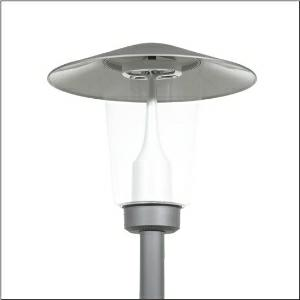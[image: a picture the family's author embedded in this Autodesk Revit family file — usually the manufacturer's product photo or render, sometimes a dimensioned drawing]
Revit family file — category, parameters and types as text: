
# Revit family: pilzleuchte_iq___st1_2a_5xa5235kf14h_dd17
name_source: partatom
category: Lighting Fixtures
units: mm (PartAtom-declared; Revit-internal decimal feet)

## family parameters
Cut with Voids When Loaded = No
Host = Face
Light Source = No
Part Type = Normal
Room Calculation Point = No
Round Connector Dimension = Use Diameter
Shared = No

## types (1)
- --- (1 x LED, 1550 lm, 10 W, 4000K)
    Apparent Load = 10 VA
    CIE Flux Codes = 24 61 93 98 100
    Color Rendering = 70
    Color Temperature = 4000K
    Default Elevation = 1800 mm
    Description = Mushroom Luminaire iQ, mast luminaire, Module 540 iQ-SR, primary light control with 3 zone facetted reflector, of plastic, silver coated, highly specular, structured, primary optical cover: cover, of PMMA, transparent, light distribution: ST1.2a, light emission: direct distribution, primary light characteristic: asymmetric, installation type: post-top, LED, High Power LED, rated luminous flux: 1.550lm, luminous efficacy: 155lm/W, light colour: 740, colour temperature: 4000K, control gear: iQ Street-Remote, control: pre-setting: logarithmic dimming characteristic, Street-Remote, Auto-Match, Temp-Guard, Lumen-Switch, Night-Set, Smart-Wire, Light-Fading, Desk-Remote (wireless, voltage-free reading and setting of iQ features in the workshop via application-optimized NFC function/RFID function), optimised constant luminous flux control (CLO 2.0), with terminal, 6-pole, max. 2.5mm², mains connection: 230..240V, AC, 50/60Hz, start of lifetime: 10W, end of service life: 10W, reduction: 5W, luminaire housing, upper part, of glass-fibre reinforced polyester, coated, Siteco® metallic grey (DB 702S), diameter: 650mm, height: 586mm, spigot size: d x l = 76 x 70mm (post-top) | with reducer (optional accessory) 60 x 70mm, mounting height: 3..5m, post-top mast mounting element, of diecast aluminium, coated, Siteco® metallic grey (DB 702S), Module 540 iQ-SR, traffic white (RAL 9016), equipment: standard, protection rating (complete): IP65, insulation class (complete): insulation class II (safety insulation), certification: CE, ENEC, VDE, packaging unit: 1 piece

Light Distribution: ST1.2a
    Height = 586 mm
    Lamp = 1 x LED
    Lamp Light Flux = 1550 lm
    Lamp Power = 10 W
    Lamp count = 1
    Length = 650 mm
    Luminous efficacy = 155 lm/W
    Manufacturer = Siteco
    ModVariant = No
    Model = 5XA5235KF14H
    Number of Poles = 1
    OnlyDefault = Yes
    Power Factor = 1
    Product Name = Pilzleuchte iQ | ST1.2a
    Product group = mast luminaire | pylon top
    ProductGroupID = 6100
    Protection Class = Protection class II
    Protection Degree = IP 65
    RLX_Detail_Level = 1
    RLX_Emergency_Light_Flux = 0 lm
    RLX_Emergency_Type = 0
    RLX_Emergency_Type_DB = No
    RlxData = <blob elided: 127733 chars, md5=eb1f7e54>
    Socket = socket
    Standby Power = 0 W
    System Light Flux = 1550 lm
    System Power = 10 W
    Type Comments = factory setting: luminous flux: 100 % | dim-lin: 254 | 401 mA
    Type Image = l_1006077.jpg
    URL = http://relux.com
    VarID = @adj_160211
    Voltage = 0 V
    Weight = 0.00 kg
    Width = 0 mm  [stored 0 ft]

note: [stored X ft] marks values corroborated as IEEE doubles in the binary element streams (Revit-internal decimal feet)

## geometry (parser evidence)
native form markers: Blend x4, Sweep x11
no freeform markers — native parametric forms only
